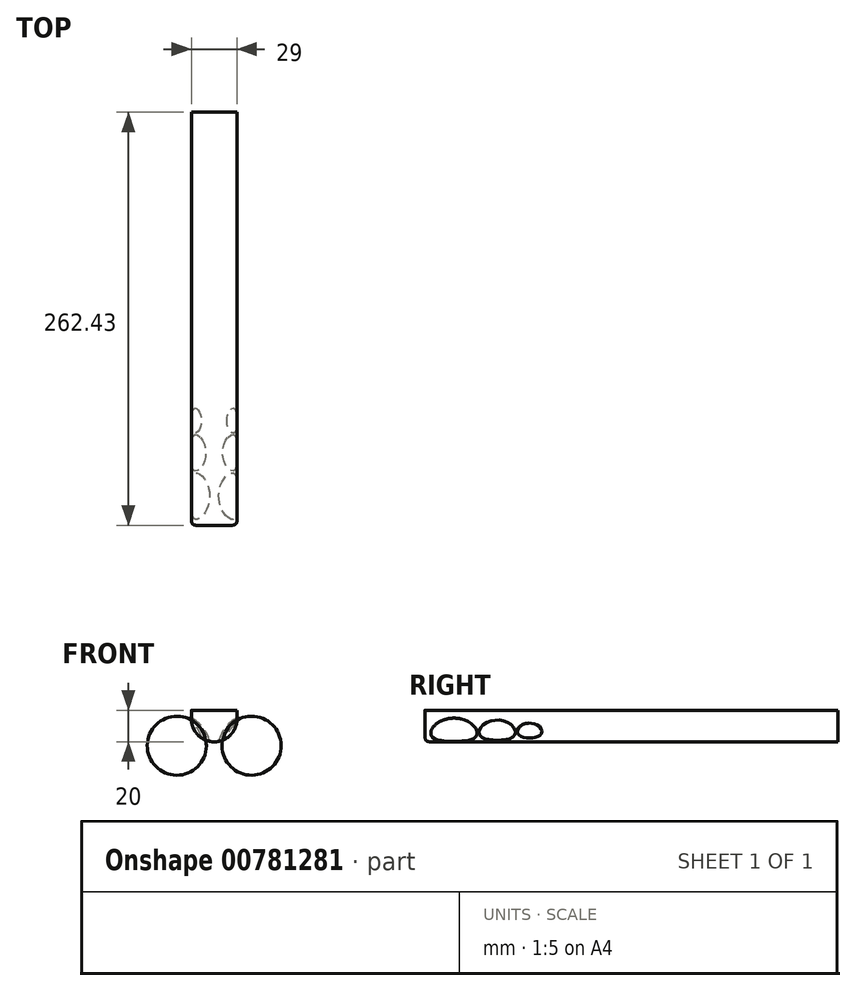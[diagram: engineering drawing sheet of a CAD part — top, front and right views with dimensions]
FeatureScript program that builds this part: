
annotation { "Feature Type Name" : "Feature", "Feature Type Description" : "" }
export const myFeature = defineFeature(function(context is Context, id is Id, definition is map)
    precondition{}
    {
        {
            var Q0;
            Q0=qCreatedBy(makeId("Front.planeOp"),FACE);
            var sketch = newSketch(context, id + "F0", { "sketchPlane" : qUnion([Q0])});
            skPoint(sketch, "E0.middle", {"position": v(0, 0) * mm});
            skLineSegment(sketch, "E1.bottom", {"start": v(0, -20) * mm, "end": v(0, -20) * mm});
            skLineSegment(sketch, "E2", {"start": v(14.5, 0) * mm, "end": v(-14.5, 0) * mm});
            skLineSegment(sketch, "E3", {"start": v(14.5, 0) * mm, "end": v(14.5, -5.5) * mm});
            skLineSegment(sketch, "E4", {"start": v(-14.5, 0) * mm, "end": v(-14.5, -5.5) * mm});
            skPoint(sketch, "E5.visualSharp", {"position": v(14.5, -20) * mm});
            skArc(sketch, "E5.filletArc", {"start": v(0, -20) * mm, "mid": v(10.25, -15.75) * mm, "end": v(14.5, -5.5) * mm});
            skPoint(sketch, "E6.visualSharp", {"position": v(-14.5, -20) * mm});
            skArc(sketch, "E6.filletArc", {"start": v(-14.5, -5.5) * mm, "mid": v(-10.25, -15.75) * mm, "end": v(0, -20) * mm});
            skSolve(sketch);
        }
        {
            var Q0;
            Q0=makeQuery(id+"F0.imprint","IMPRINT",FACE,{"disambiguationData":[TD([[makeQuery(id+"F0.imprint","IMPRINT",EDGE,{"derivedFrom":sQuery(id+"F0.wireOp",EDGE,"E2")}),1.0]])]});
            extrude(context, id + "F1", {"entities" : qUnion([Q0]), "depth" : ((515.86 / 2) + 4.5) * mm, "offsetDistance" : 25 * mm});
        }
        {
            var Q0;
            Q0=qCreatedBy(makeId("Top.planeOp"),FACE);
            var sketch = newSketch(context, id + "F2", { "sketchPlane" : qUnion([Q0])});
            skPoint(sketch, "E7.third.point", {"position": v(-15, 0) * mm});
            skArc(sketch, "E8", {"start": v(0, 15) * mm, "mid": v(-15, 0) * mm, "end": v(0, -15) * mm});
            skLineSegment(sketch, "E9", {"start": v(-15, 0) * mm, "end": v(0, 0) * mm, "construction": true});
            skLineSegment(sketch, "E10", {"start": v(0, -15) * mm, "end": v(0, 0) * mm});
            skLineSegment(sketch, "E11", {"start": v(0, 0) * mm, "end": v(0, 15) * mm});
            skSolve(sketch);
        }
        {
            var Q0;
            Q0=makeQuery(id+"F2.imprint","IMPRINT",FACE,{"disambiguationData":[TD([[makeQuery(id+"F2.imprint","IMPRINT",EDGE,{"derivedFrom":sQuery(id+"F2.wireOp",EDGE,"E8")}),1.0]])]});
            var Q1;
            Q1=sQuery(id+"F2.wireOp",EDGE,"E10");
            revolve(context, id + "F3", {"surfaceOperationType" : NewSurfaceOperationType.NEW, "entities" : qUnion([Q0]), "axis" : qUnion([Q1]), "revolveType" : RevolveType.FULL});
        }
        {
            var Q0;
            Q0=makeQuery(id+"F3.opRevolve","SWEPT_BODY",BODY,{"disambiguationData":[OSD([sQuery(id+"F2.wireOp",EDGE,"E8"),sQuery(id+"F2.wireOp",EDGE,"E10"),sQuery(id+"F2.wireOp",EDGE,"E11")])]});
            var Q1;
            Q1=qCreatedBy(makeId("Origin.pointOp"),VERTEX);
            transform(context, id + "F4", {"entities" : qUnion([Q0]), "transformType" : TransformType.SCALE_UNIFORMLY, "scale" : 1.25, "scalePoint" : qUnion([Q1]), "makeCopy" : true});
        }
        {
            var Q0;
            Q0=makeQuery(id+"F3.opRevolve","SWEPT_BODY",BODY,{"disambiguationData":[OSD([sQuery(id+"F2.wireOp",EDGE,"E8"),sQuery(id+"F2.wireOp",EDGE,"E10"),sQuery(id+"F2.wireOp",EDGE,"E11")])]});
            var Q1;
            Q1=qCreatedBy(makeId("Origin.pointOp"),VERTEX);
            var Q2;
            Q2=qCreatedBy(makeId("Origin.pointOp"),VERTEX);
            transform(context, id + "F5", {"entities" : qUnion([Q0]), "transformType" : TransformType.SCALE_UNIFORMLY, "scale" : 1.5, "scalePoint" : qUnion([Q2]), "makeCopy" : true});
        }
        {
            var Q0;
            Q0=makeQuery(id+"F3.opRevolve","SWEPT_BODY",BODY,{"disambiguationData":[OSD([sQuery(id+"F2.wireOp",EDGE,"E8"),sQuery(id+"F2.wireOp",EDGE,"E10"),sQuery(id+"F2.wireOp",EDGE,"E11")])]});
            var Q1;
            Q1=makeQuery(id+"F4.opPattern","COPY",BODY,{"derivedFrom":makeQuery(id+"F3.opRevolve","SWEPT_BODY",BODY,{"disambiguationData":[OSD([sQuery(id+"F2.wireOp",EDGE,"E8"),sQuery(id+"F2.wireOp",EDGE,"E10"),sQuery(id+"F2.wireOp",EDGE,"E11")])]}),"instanceName":"1"});
            var Q2;
            Q2=makeQuery(id+"F5.opPattern","COPY",BODY,{"derivedFrom":makeQuery(id+"F3.opRevolve","SWEPT_BODY",BODY,{"disambiguationData":[OSD([sQuery(id+"F2.wireOp",EDGE,"E8"),sQuery(id+"F2.wireOp",EDGE,"E10"),sQuery(id+"F2.wireOp",EDGE,"E11")])]}),"instanceName":"1"});
            var Q3;
            Q3=makeQuery(id+"F1.opExtrude","SWEPT_EDGE",EDGE,{"disambiguationData":[OSD([sQuery(id+"F0.wireOp",EDGE,"E3"),sQuery(id+"F0.wireOp",EDGE,"E5.filletArc")])]});
            transform(context, id + "F6", {"entities" : qUnion([Q0, Q1, Q2]), "transformType" : TransformType.TRANSLATION_3D, "dx" : 18.75 * mm, "dy" : 0 * mm, "dz" : -15 * mm, "makeCopy" : false});
        }
        {
            var Q0;
            Q0=makeQuery(id+"F3.opRevolve","SWEPT_BODY",BODY,{"disambiguationData":[OSD([sQuery(id+"F2.wireOp",EDGE,"E8"),sQuery(id+"F2.wireOp",EDGE,"E10"),sQuery(id+"F2.wireOp",EDGE,"E11")])]});
            transform(context, id + "F7", {"entities" : qUnion([Q0]), "transformType" : TransformType.TRANSLATION_3D, "dx" : 4 * mm, "dy" : -195.93 * mm, "dz" : -5.5 * mm, "makeCopy" : false});
        }
        {
            var Q0;
            Q0=makeQuery(id+"F4.opPattern","COPY",BODY,{"derivedFrom":makeQuery(id+"F3.opRevolve","SWEPT_BODY",BODY,{"disambiguationData":[OSD([sQuery(id+"F2.wireOp",EDGE,"E8"),sQuery(id+"F2.wireOp",EDGE,"E10"),sQuery(id+"F2.wireOp",EDGE,"E11")])]}),"instanceName":"1"});
            transform(context, id + "F8", {"entities" : qUnion([Q0]), "transformType" : TransformType.TRANSLATION_3D, "dx" : 5 * mm, "dy" : -216.43 * mm, "dz" : -7.5 * mm, "makeCopy" : false});
        }
        {
            var Q0;
            Q0=makeQuery(id+"F5.opPattern","COPY",BODY,{"derivedFrom":makeQuery(id+"F3.opRevolve","SWEPT_BODY",BODY,{"disambiguationData":[OSD([sQuery(id+"F2.wireOp",EDGE,"E8"),sQuery(id+"F2.wireOp",EDGE,"E10"),sQuery(id+"F2.wireOp",EDGE,"E11")])]}),"instanceName":"1"});
            transform(context, id + "F9", {"entities" : qUnion([Q0]), "transformType" : TransformType.TRANSLATION_3D, "dx" : 6 * mm, "dy" : -243.93 * mm, "dz" : -10 * mm, "makeCopy" : false});
        }
        {
            var Q0;
            Q0=makeQuery(id+"F3.opRevolve","SWEPT_BODY",BODY,{"disambiguationData":[OSD([sQuery(id+"F2.wireOp",EDGE,"E8"),sQuery(id+"F2.wireOp",EDGE,"E10"),sQuery(id+"F2.wireOp",EDGE,"E11")])]});
            var Q1;
            Q1=makeQuery(id+"F4.opPattern","COPY",BODY,{"derivedFrom":makeQuery(id+"F3.opRevolve","SWEPT_BODY",BODY,{"disambiguationData":[OSD([sQuery(id+"F2.wireOp",EDGE,"E8"),sQuery(id+"F2.wireOp",EDGE,"E10"),sQuery(id+"F2.wireOp",EDGE,"E11")])]}),"instanceName":"1"});
            var Q2;
            Q2=makeQuery(id+"F5.opPattern","COPY",BODY,{"derivedFrom":makeQuery(id+"F3.opRevolve","SWEPT_BODY",BODY,{"disambiguationData":[OSD([sQuery(id+"F2.wireOp",EDGE,"E8"),sQuery(id+"F2.wireOp",EDGE,"E10"),sQuery(id+"F2.wireOp",EDGE,"E11")])]}),"instanceName":"1"});
            var Q3;
            Q3=qCreatedBy(makeId("Right.planeOp"),FACE);
            mirror(context, id + "F10", {"entities" : qUnion([Q0, Q1, Q2]), "mirrorPlane" : qUnion([Q3])});
        }
        {
            var Q0;
            Q0=makeQuery(id+"F3.opRevolve","SWEPT_BODY",BODY,{"disambiguationData":[OSD([sQuery(id+"F2.wireOp",EDGE,"E8"),sQuery(id+"F2.wireOp",EDGE,"E10"),sQuery(id+"F2.wireOp",EDGE,"E11")])]});
            var Q1;
            Q1=makeQuery(id+"F4.opPattern","COPY",BODY,{"derivedFrom":makeQuery(id+"F3.opRevolve","SWEPT_BODY",BODY,{"disambiguationData":[OSD([sQuery(id+"F2.wireOp",EDGE,"E8"),sQuery(id+"F2.wireOp",EDGE,"E10"),sQuery(id+"F2.wireOp",EDGE,"E11")])]}),"instanceName":"1"});
            var Q2;
            Q2=makeQuery(id+"F5.opPattern","COPY",BODY,{"derivedFrom":makeQuery(id+"F3.opRevolve","SWEPT_BODY",BODY,{"disambiguationData":[OSD([sQuery(id+"F2.wireOp",EDGE,"E8"),sQuery(id+"F2.wireOp",EDGE,"E10"),sQuery(id+"F2.wireOp",EDGE,"E11")])]}),"instanceName":"1"});
            var Q3;
            Q3=makeQuery(id+"F10.opPattern","COPY",BODY,{"derivedFrom":makeQuery(id+"F3.opRevolve","SWEPT_BODY",BODY,{"disambiguationData":[OSD([sQuery(id+"F2.wireOp",EDGE,"E8"),sQuery(id+"F2.wireOp",EDGE,"E10"),sQuery(id+"F2.wireOp",EDGE,"E11")])]}),"instanceName":"1"});
            var Q4;
            Q4=makeQuery(id+"F10.opPattern","COPY",BODY,{"derivedFrom":makeQuery(id+"F4.opPattern","COPY",BODY,{"derivedFrom":makeQuery(id+"F3.opRevolve","SWEPT_BODY",BODY,{"disambiguationData":[OSD([sQuery(id+"F2.wireOp",EDGE,"E8"),sQuery(id+"F2.wireOp",EDGE,"E10"),sQuery(id+"F2.wireOp",EDGE,"E11")])]}),"instanceName":"1"}),"instanceName":"1"});
            var Q5;
            Q5=makeQuery(id+"F10.opPattern","COPY",BODY,{"derivedFrom":makeQuery(id+"F5.opPattern","COPY",BODY,{"derivedFrom":makeQuery(id+"F3.opRevolve","SWEPT_BODY",BODY,{"disambiguationData":[OSD([sQuery(id+"F2.wireOp",EDGE,"E8"),sQuery(id+"F2.wireOp",EDGE,"E10"),sQuery(id+"F2.wireOp",EDGE,"E11")])]}),"instanceName":"1"}),"instanceName":"1"});
            var Q6;
            Q6=makeQuery(id+"F1.opExtrude","SWEPT_BODY",BODY,{"disambiguationData":[OSD([sQuery(id+"F0.wireOp",EDGE,"E2"),sQuery(id+"F0.wireOp",EDGE,"E3"),sQuery(id+"F0.wireOp",EDGE,"E4"),sQuery(id+"F0.wireOp",EDGE,"E5.filletArc"),sQuery(id+"F0.wireOp",EDGE,"E6.filletArc")])]});
            booleanBodies(context, id + "F11", {"operationType" : BooleanOperationType.SUBTRACTION, "tools" : qUnion([Q0, Q1, Q2, Q3, Q4, Q5]), "targets" : qUnion([Q6])});
        }
        {
            var Q0;
            Q0=makeQuery(id+"F1.opExtrude","CAP_EDGE",EDGE,{"disambiguationData":[OSD([sQuery(id+"F0.wireOp",EDGE,"E3")])],"isStart":false});
            var Q1;
            {var subQ0=sQuery(id+"F0.wireOp",EDGE,"E6.filletArc");var subQ1=sQuery(id+"F0.wireOp",EDGE,"E5.filletArc");var subQ2=sQuery(id+"F0.wireOp",EDGE,"E3");Q1=makeQuery(id+"F11.opBoolean","SPLIT",EDGE,{"disambiguationData":[TD([makeQuery(id+"F1.opExtrude","CAP_FACE",FACE,{"disambiguationData":[OSD([sQuery(id+"F0.wireOp",EDGE,"E2"),subQ2,sQuery(id+"F0.wireOp",EDGE,"E4"),subQ1,subQ0])],"isStart":false}),makeQuery(id+"F1.opExtrude","SWEPT_FACE",FACE,{"disambiguationData":[OSD([subQ2])]}),makeQuery(id+"F1.opExtrude","SWEPT_FACE",FACE,{"disambiguationData":[OSD([subQ1,subQ0])]}),makeQuery(id+"F5.opPattern","COPY",FACE,{"derivedFrom":makeQuery(id+"F3.opRevolve","SWEPT_FACE",FACE,{"disambiguationData":[OSD([sQuery(id+"F2.wireOp",EDGE,"E8")])]}),"instanceName":"1"})])],"derivedFrom":makeQuery(id+"F1.opExtrude","CAP_EDGE",EDGE,{"disambiguationData":[OSD([subQ1,subQ0])],"isStart":false})});}
            var Q2;
            {var subQ0=sQuery(id+"F0.wireOp",EDGE,"E6.filletArc");var subQ1=sQuery(id+"F0.wireOp",EDGE,"E5.filletArc");var subQ2=makeQuery(id+"F5.opPattern","COPY",FACE,{"derivedFrom":makeQuery(id+"F3.opRevolve","SWEPT_FACE",FACE,{"disambiguationData":[OSD([sQuery(id+"F2.wireOp",EDGE,"E8")])]}),"instanceName":"1"});Q2=makeQuery(id+"F11.opBoolean","SPLIT",EDGE,{"disambiguationData":[TD([makeQuery(id+"F1.opExtrude","CAP_FACE",FACE,{"disambiguationData":[OSD([sQuery(id+"F0.wireOp",EDGE,"E2"),sQuery(id+"F0.wireOp",EDGE,"E3"),sQuery(id+"F0.wireOp",EDGE,"E4"),subQ1,subQ0])],"isStart":false}),makeQuery(id+"F1.opExtrude","SWEPT_FACE",FACE,{"disambiguationData":[OSD([subQ1,subQ0])]}),subQ2,makeQuery(id+"F10.opPattern","COPY",FACE,{"derivedFrom":subQ2,"instanceName":"1"})])],"derivedFrom":makeQuery(id+"F1.opExtrude","CAP_EDGE",EDGE,{"disambiguationData":[OSD([subQ1,subQ0])],"isStart":false})});}
            var Q3;
            Q3=makeQuery(id+"F1.opExtrude","CAP_EDGE",EDGE,{"disambiguationData":[OSD([sQuery(id+"F0.wireOp",EDGE,"E4")])],"isStart":false});
            var Q4;
            {var subQ0=sQuery(id+"F0.wireOp",EDGE,"E6.filletArc");var subQ1=sQuery(id+"F0.wireOp",EDGE,"E5.filletArc");var subQ2=sQuery(id+"F0.wireOp",EDGE,"E4");Q4=makeQuery(id+"F11.opBoolean","SPLIT",EDGE,{"disambiguationData":[TD([makeQuery(id+"F1.opExtrude","CAP_FACE",FACE,{"disambiguationData":[OSD([sQuery(id+"F0.wireOp",EDGE,"E2"),sQuery(id+"F0.wireOp",EDGE,"E3"),subQ2,subQ1,subQ0])],"isStart":false}),makeQuery(id+"F1.opExtrude","SWEPT_FACE",FACE,{"disambiguationData":[OSD([subQ2])]}),makeQuery(id+"F1.opExtrude","SWEPT_FACE",FACE,{"disambiguationData":[OSD([subQ1,subQ0])]}),makeQuery(id+"F10.opPattern","COPY",FACE,{"derivedFrom":makeQuery(id+"F5.opPattern","COPY",FACE,{"derivedFrom":makeQuery(id+"F3.opRevolve","SWEPT_FACE",FACE,{"disambiguationData":[OSD([sQuery(id+"F2.wireOp",EDGE,"E8")])]}),"instanceName":"1"}),"instanceName":"1"})])],"derivedFrom":makeQuery(id+"F1.opExtrude","CAP_EDGE",EDGE,{"disambiguationData":[OSD([subQ1,subQ0])],"isStart":false})});}
            fillet(context, id + "F12", {"entities" : qUnion([Q0, Q1, Q2, Q3, Q4]), "radius" : 4 * mm, "rho" : 0.6, "crossSection" : FilletCrossSection.CONIC, "allowEdgeOverflow" : false});
        }
    });
